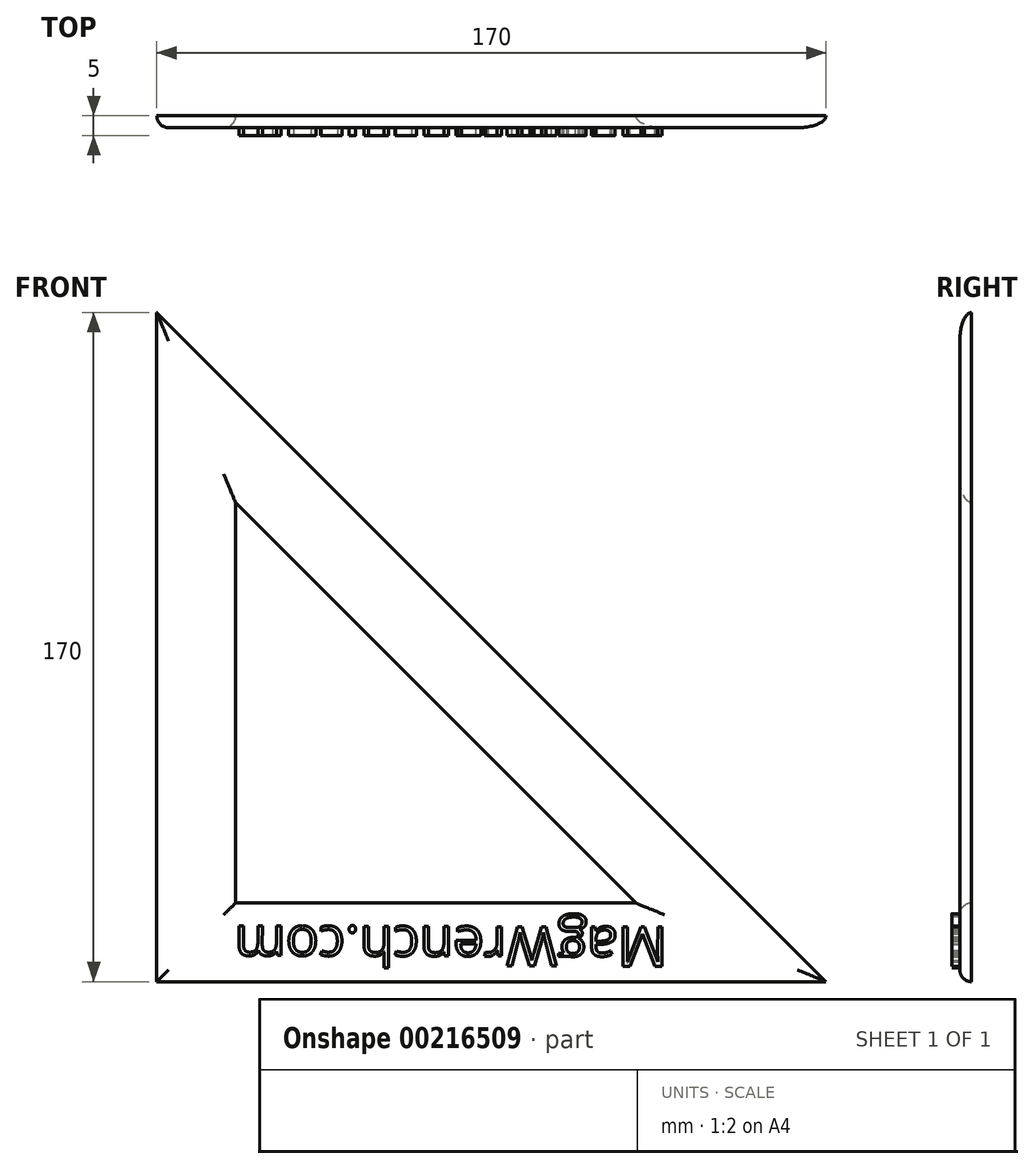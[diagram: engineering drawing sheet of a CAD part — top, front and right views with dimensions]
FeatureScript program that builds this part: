
annotation { "Feature Type Name" : "Feature", "Feature Type Description" : "" }
export const myFeature = defineFeature(function(context is Context, id is Id, definition is map)
    precondition{}
    {
        {
            var Q0;
            Q0=qCreatedBy(makeId("Front.planeOp"),FACE);
            var sketch = newSketch(context, id + "F0", { "sketchPlane" : qUnion([Q0])});
            skLineSegment(sketch, "E0", {"start": v(0, 101.72) * mm, "end": v(0, 0) * mm});
            skLineSegment(sketch, "E1", {"start": v(0, 0) * mm, "end": v(101.72, 0) * mm});
            skLineSegment(sketch, "E2", {"start": v(101.72, 0) * mm, "end": v(0, 101.72) * mm});
            skLineSegment(sketch, "E3.0", {"start": v(-20, -20) * mm, "end": v(150, -20) * mm});
            skLineSegment(sketch, "E3.1", {"start": v(-20, 150) * mm, "end": v(-20, -20) * mm});
            skLineSegment(sketch, "E3.2", {"start": v(150, -20) * mm, "end": v(-20, 150) * mm});
            skSolve(sketch);
        }
        {
            var Q0;
            Q0=makeQuery(id+"F0.imprint","IMPRINT",FACE,{"disambiguationData":[TD([[makeQuery(id+"F0.imprint","IMPRINT",EDGE,{"derivedFrom":sQuery(id+"F0.wireOp",EDGE,"E0")}),-1.0]])]});
            extrude(context, id + "F1", {"entities" : qUnion([Q0]), "depth" : 3 * mm});
        }
        {
            var Q0;
            Q0=makeQuery(id+"F1.opExtrude","CAP_FACE",FACE,{"disambiguationData":[OSD([sQuery(id+"F0.wireOp",EDGE,"E0"),sQuery(id+"F0.wireOp",EDGE,"E1"),sQuery(id+"F0.wireOp",EDGE,"E2"),sQuery(id+"F0.wireOp",EDGE,"E3.0"),sQuery(id+"F0.wireOp",EDGE,"E3.1"),sQuery(id+"F0.wireOp",EDGE,"E3.2")])],"isStart":false});
            fillet(context, id + "F2", {"entities" : qUnion([Q0]), "radius" : 3 * mm, "tangentPropagation" : true, "allowEdgeOverflow" : false});
        }
        {
            var Q0;
            Q0=makeQuery(id+"F1.opExtrude","CAP_FACE",FACE,{"disambiguationData":[OSD([sQuery(id+"F0.wireOp",EDGE,"E0"),sQuery(id+"F0.wireOp",EDGE,"E1"),sQuery(id+"F0.wireOp",EDGE,"E2"),sQuery(id+"F0.wireOp",EDGE,"E3.0"),sQuery(id+"F0.wireOp",EDGE,"E3.1"),sQuery(id+"F0.wireOp",EDGE,"E3.2")])],"isStart":false});
            var sketch = newSketch(context, id + "F3", { "sketchPlane" : qUnion([Q0])});
            skText(sketch, "E4", { "text": "MagWrench.com", "fontName": "OpenSans-Regular.ttf"});
            const initialGuessF3  = {"E4": [0.1097, -0.00612, -1, 0.00248, 0.01004]};
            skSetInitialGuess(sketch, initialGuessF3);
            skSolve(sketch);
        }
        {
            var Q0;
            Q0 = qSketchRegion(id + "F3", true);
            extrude(context, id + "F4", {"entities" : qUnion([Q0]), "operationType" : NewBodyOperationType.ADD, "depth" : 2 * mm});
        }
    });
